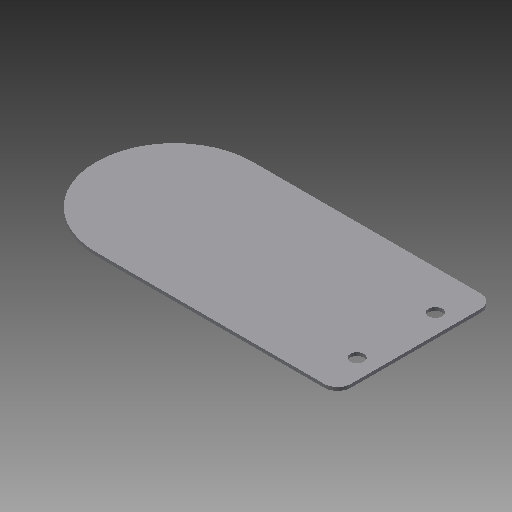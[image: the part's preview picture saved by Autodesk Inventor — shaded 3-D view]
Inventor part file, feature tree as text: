
AUTODESK INVENTOR PART (.ipt)
format: ipt  version: 2018 (Build 220112000, 112)  size: 94,720 bytes
history: native  units: mm
features: mirror x2, extrude x1, hole x1
ambient origin geometry x8: Origin, YZ Plane, XZ Plane, XY Plane, X Axis, Y Axis, Z Axis, Center Point
bodies: Volumenkörper1 (feature_tree)
feature tree (4):
  extrude  "Extrusion1"  Depth=24.0mm
  mirror  "Spiegeln1"
  hole  "Bohrung1"  [1 undecoded]
  mirror  "Spiegeln2"
note: 1 required parameter value undecoded (feature->parameter linkage not recoverable at this tier; creation-order binding heuristic only, values carry confidence <= 0.55)
